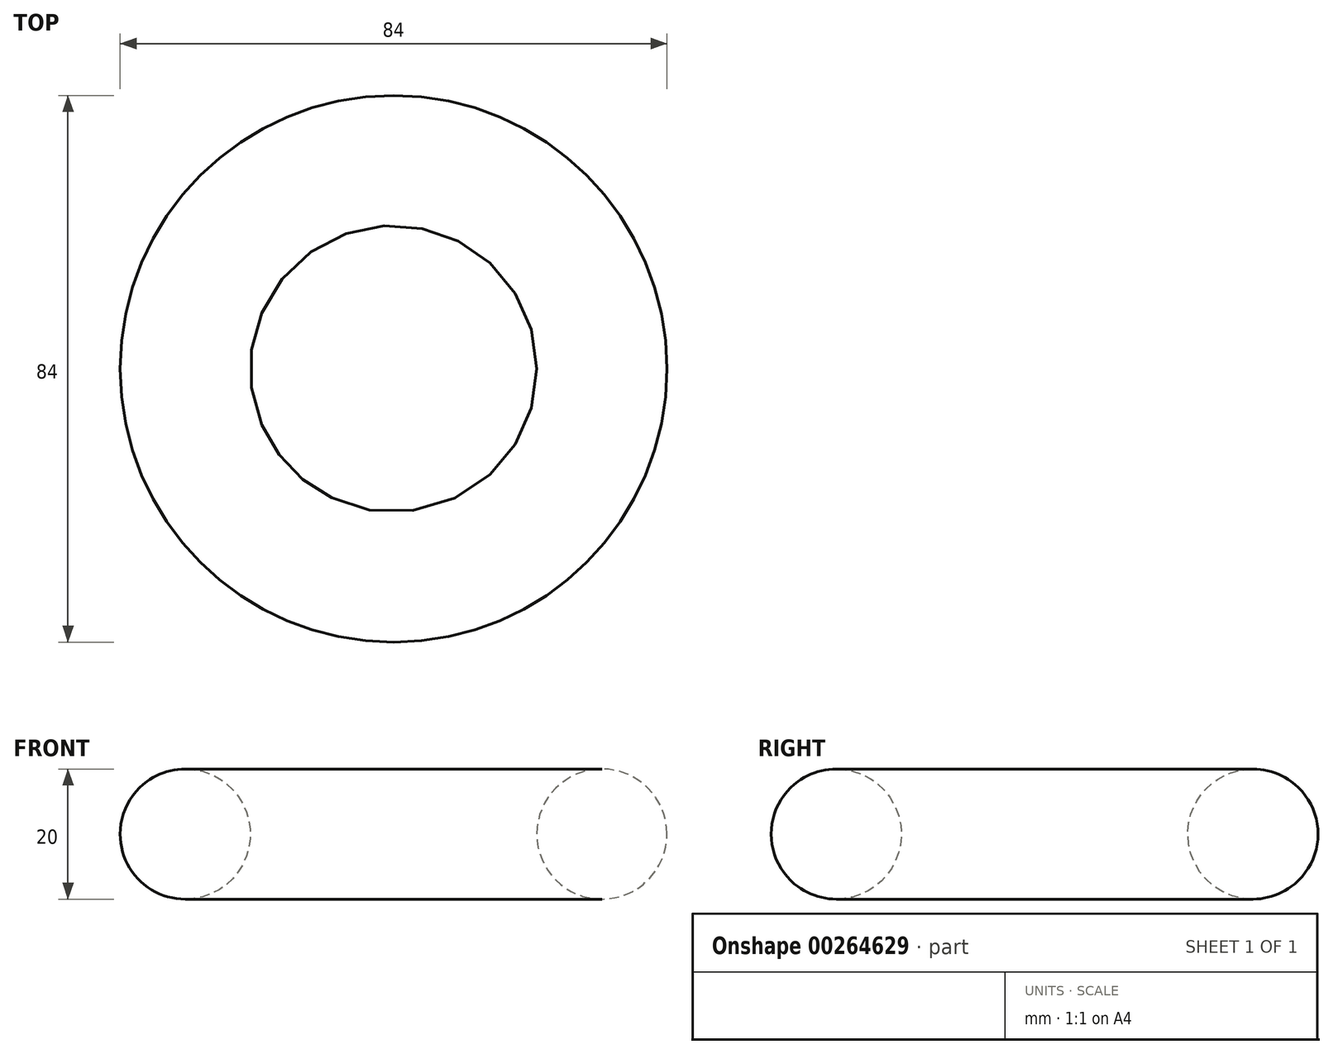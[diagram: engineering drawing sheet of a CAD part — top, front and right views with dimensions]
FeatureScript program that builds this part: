
annotation { "Feature Type Name" : "Feature", "Feature Type Description" : "" }
export const myFeature = defineFeature(function(context is Context, id is Id, definition is map)
    precondition{}
    {
        {
            var Q0;
            Q0=qCreatedBy(makeId("Front.planeOp"),FACE);
            var sketch = newSketch(context, id + "F0", { "sketchPlane" : qUnion([Q0])});
            skCircle(sketch, "E0", {"center": v(32, 0) * mm, "radius": 10 * mm});
            skLineSegment(sketch, "E1", {"start": v(0, 35.88) * mm, "end": v(0, -52.66) * mm, "construction": true});
            skSolve(sketch);
        }
        {
            var Q0;
            Q0=makeQuery(id+"F0.imprint","IMPRINT",FACE,{"disambiguationData":[TD([[makeQuery(id+"F0.imprint","IMPRINT",EDGE,{"derivedFrom":sQuery(id+"F0.wireOp",EDGE,"E0")}),1.0]])]});
            var Q1;
            Q1=sQuery(id+"F0.wireOp",EDGE,"E1");
            var Q2;
            Q2=sQuery(id+"F0.wireOp",EDGE,"E1");
            revolve(context, id + "F1", {"entities" : qUnion([Q0]), "surfaceEntities" : qUnion([Q1]), "axis" : qUnion([Q2]), "revolveType" : RevolveType.FULL});
        }
    });
